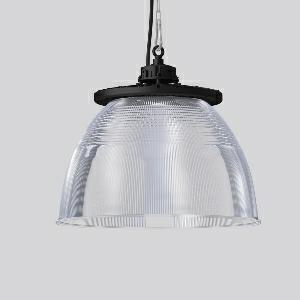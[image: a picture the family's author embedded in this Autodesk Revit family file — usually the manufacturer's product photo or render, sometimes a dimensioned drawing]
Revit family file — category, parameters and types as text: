
# Revit family: industrial_hall_refraktor_921704_003_f23c
name_source: partatom
category: Lighting Fixtures
units: mm (PartAtom-declared; Revit-internal decimal feet)

## family parameters
Cut with Voids When Loaded = No
Host = Face
Light Source = No
Part Type = Normal
Room Calculation Point = No
Round Connector Dimension = Use Diameter
Shared = No

## types (1)
- INDUSTRIAL HALL refraktor (1 x LED Modul 840, 11700 lm, 4000)
    Apparent Load = 85 VA
    CIE Flux Codes = 88 97 99 94 100
    Color Rendering = 80
    Color Temperature = 4000
    Default Elevation = 1800 mm
    Description = Series: INDUSTRIAL HALL
Round highbay luminaire for chain or cable suspension. Robust housing made of die-cast aluminium with eye ring, powder coated. Vertical cooling ribs ensure constant heat dissipation for optimal thermal management. Diffuser made of clear, non-reflecting, single pane safety glass (toughened glass). Refractor: PMMA, transparent. Primary light control with high-performance wide-area LEDs and reflector made of plastic (PMMA) for optimum glare limitation: RUG <19. Easy to install thanks to 1-point suspension. Suitable for chain or steel cable suspension (to be provided on site). With power cord (1.5 m). Ceiling- and wall-mounting bracket available as accessory. Luminaire with limited surface temperature in accordance with EN 60598-2-24 for use in environments in which a deposit of conductive dust on the luminaire can be expected. Qualified for use in the food and drink industry. 
Colour: deep black, matt (RAL 9005)
Diameter: 570 mm
Height: 509 mm
Lamp: LED
Socket: without socket
Colour temperature: 4000K
Colour rendering index (CRI): 80
System power: 85 W
Rated luminous flux: 11700 lm
Luminous efficiency: 138 lm/W
Control gear: Regulated power supply
Protection class: I
Type of protection: IP 65
    Height = 509 mm
    Lamp = 1 x LED Modul 840
    Lamp Light Flux = 11700 lm
    Lamp count = 1
    Length = 570 mm
    Lifetime = 50000 h
    Luminous efficacy = 138 lm/W
    Manufacturer = RZB
    ModVariant = No
    Model = 921704.003
    Mounting Place = Ceiling
    Mounting Type = Pendant
    Number of Poles = 1
    OnlyDefault = Yes
    Power Factor = 1
    Product Name = INDUSTRIAL HALL refraktor
    Product group = Pendant commercial luminaires
    ProductGroupID = 903
    Protection Class = Protection class I
    Protection Degree = Degree of protection
    RLX_Detail_Level = 1
    RLX_Emergency_Light_Flux = 0 lm
    RLX_Emergency_Type = 0
    RLX_Emergency_Type_DB = No
    RlxData = <blob elided: 253317 chars, md5=f6f6430e>
    Socket = socket
    Standby Power = 0 W
    System Light Flux = 11700 lm
    System Power = 85 W
    Type Comments = Product without accessories
    Type Image = 921704.003.jpg
    URL = http://relux.com
    VarID = ---
    Voltage = 0 V
    Weight = 0.00 kg
    Width = 0 mm  [stored 0 ft]

note: [stored X ft] marks values corroborated as IEEE doubles in the binary element streams (Revit-internal decimal feet)

## geometry (parser evidence)
native form markers: Blend x4, Sweep x14
no freeform markers — native parametric forms only
